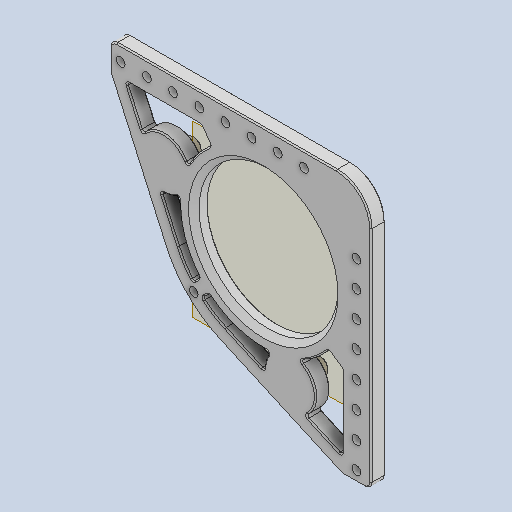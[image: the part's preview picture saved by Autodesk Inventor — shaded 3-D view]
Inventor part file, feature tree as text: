
AUTODESK INVENTOR PART (.ipt)
format: ipt  version: 2022 (Build 260153000, 153)  size: 395,776 bytes
history: native  units: in
note: dims shown in document units (in); Inventor stores cm internally (conversion verified against a paired STEP export)
features: sketch x4, other x3, plane x1
ambient origin geometry x8: Origin, YZ Plane, XZ Plane, XY Plane, X Axis, Y Axis, Z Axis, Center Point
bodies: Solid1 (feature_tree)
feature tree (8):
  other  "lower_plate_MIR.ipt"
  other  "Solid1::lower_plate_MIR.ipt"
  other  "TaggingFeature1"
  sketch  "Sketch1"  dims[d0=0.3937in]
  sketch  "Sketch4"
  sketch  "Sketch5"
  sketch  "Sketch6"
  plane  "Work Plane1"
